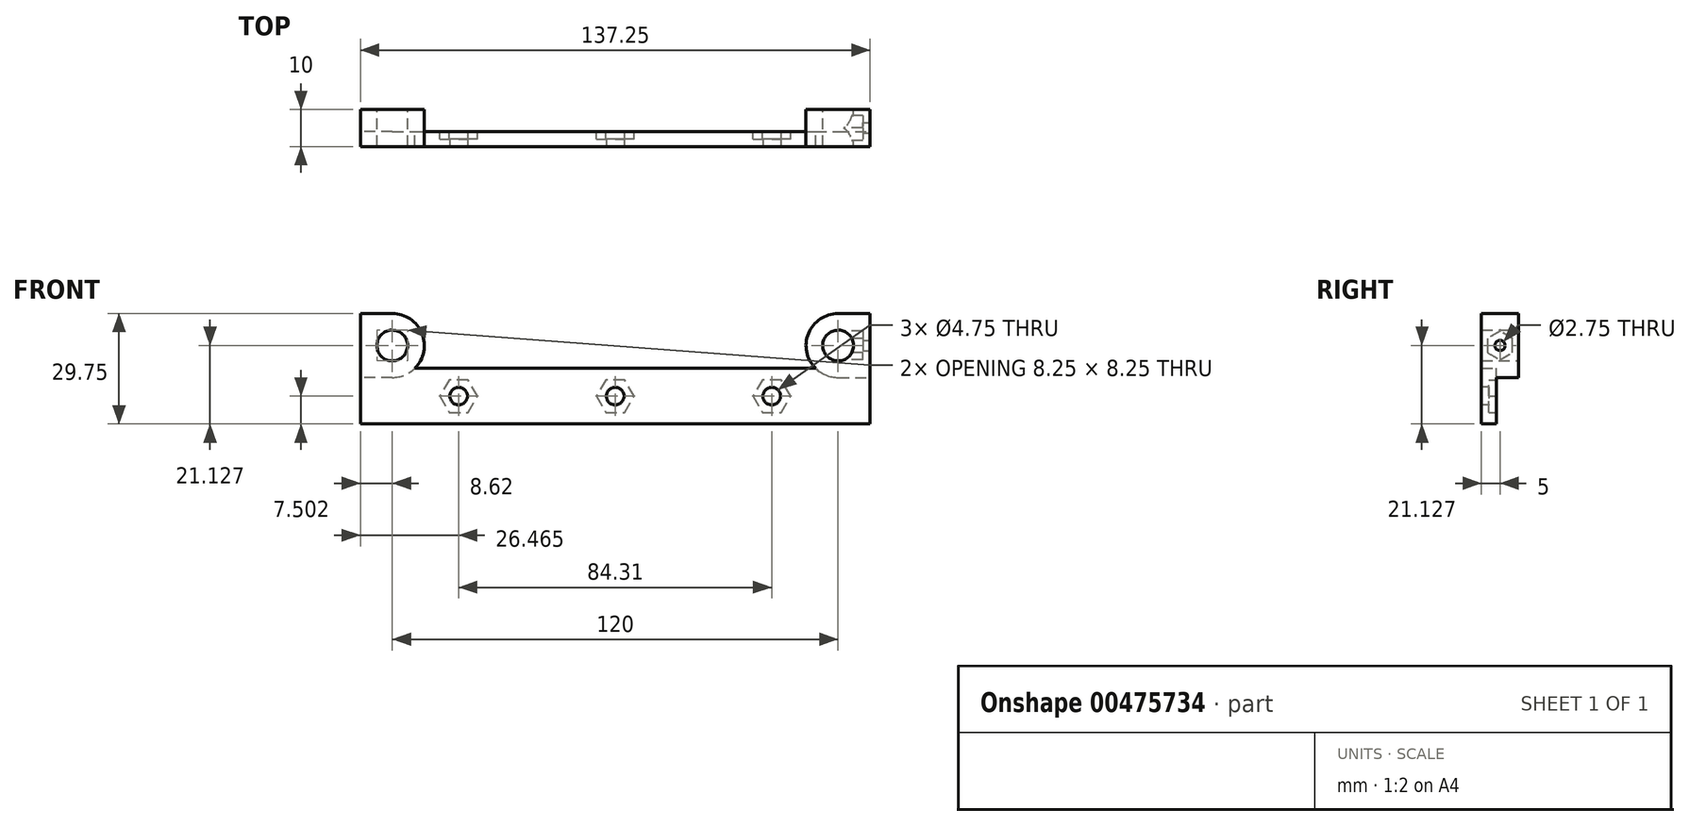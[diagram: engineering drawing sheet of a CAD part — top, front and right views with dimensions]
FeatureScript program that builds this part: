
annotation { "Feature Type Name" : "Feature", "Feature Type Description" : "" }
export const myFeature = defineFeature(function(context is Context, id is Id, definition is map)
    precondition{}
    {
        {
            var Q0;
            Q0=qCreatedBy(makeId("Front.planeOp"),FACE);
            var sketch = newSketch(context, id + "F0", { "sketchPlane" : qUnion([Q0])});
            skCircle(sketch, "E0", {"center": v(-60, 34.35) * mm, "radius": 4.12 * mm});
            skCircle(sketch, "E1", {"center": v(60, 34.35) * mm, "radius": 4.12 * mm});
            skCircle(sketch, "E2", {"center": v(-60, 34.35) * mm, "radius": 8.62 * mm});
            skCircle(sketch, "E3", {"center": v(60, 34.35) * mm, "radius": 8.62 * mm});
            skLineSegment(sketch, "E4.bottom", {"start": v(-60, 38.47) * mm, "end": v(-64.12, 38.47) * mm});
            skLineSegment(sketch, "E4.top", {"start": v(-60, 30.22) * mm, "end": v(-64.12, 30.22) * mm});
            skLineSegment(sketch, "E4.left", {"start": v(-60, 38.47) * mm, "end": v(-60, 30.22) * mm});
            skLineSegment(sketch, "E4.right", {"start": v(-64.12, 38.47) * mm, "end": v(-64.12, 30.22) * mm});
            skLineSegment(sketch, "E5.bottom", {"start": v(60, 38.47) * mm, "end": v(64.12, 38.47) * mm});
            skLineSegment(sketch, "E5.top", {"start": v(60, 30.22) * mm, "end": v(64.12, 30.22) * mm});
            skLineSegment(sketch, "E5.left", {"start": v(60, 38.47) * mm, "end": v(60, 30.22) * mm});
            skLineSegment(sketch, "E5.right", {"start": v(64.12, 38.47) * mm, "end": v(64.12, 30.22) * mm});
            skLineSegment(sketch, "E6.bottom", {"start": v(-60, 42.97) * mm, "end": v(-68.62, 42.97) * mm});
            skLineSegment(sketch, "E6.top", {"start": v(-60, 25.72) * mm, "end": v(-68.62, 25.72) * mm});
            skLineSegment(sketch, "E6.left", {"start": v(-60, 42.97) * mm, "end": v(-60, 25.72) * mm});
            skLineSegment(sketch, "E6.right", {"start": v(-68.62, 42.97) * mm, "end": v(-68.62, 25.72) * mm});
            skLineSegment(sketch, "E7.bottom", {"start": v(60, 42.97) * mm, "end": v(68.62, 42.97) * mm});
            skLineSegment(sketch, "E7.top", {"start": v(60, 25.72) * mm, "end": v(68.62, 25.72) * mm});
            skLineSegment(sketch, "E7.left", {"start": v(60, 42.97) * mm, "end": v(60, 25.72) * mm});
            skLineSegment(sketch, "E7.right", {"start": v(68.62, 42.97) * mm, "end": v(68.62, 25.72) * mm});
            skSolve(sketch);
        }
        {
            var Q0;
            Q0=qSketchRegion(id+"F0",true);
            extrude(context, id + "F1", {"entities" : qUnion([Q0]), "depth" : 5 * mm, "hasSecondDirection" : true, "secondDirectionOppositeDirection" : true, "secondDirectionDepth" : 5 * mm});
        }
        {
            var Q0;
            Q0=makeQuery(id+"F1.opExtrude","CAP_FACE",FACE,{"disambiguationData":[OSD([sQuery(id+"F0.wireOp",EDGE,"E0"),sQuery(id+"F0.wireOp",EDGE,"E2"),sQuery(id+"F0.wireOp",EDGE,"E4.bottom"),sQuery(id+"F0.wireOp",EDGE,"E4.top"),sQuery(id+"F0.wireOp",EDGE,"E4.right"),sQuery(id+"F0.wireOp",EDGE,"E6.bottom"),sQuery(id+"F0.wireOp",EDGE,"E6.top"),sQuery(id+"F0.wireOp",EDGE,"E6.right")])],"isStart":false});
            var sketch = newSketch(context, id + "F2", { "sketchPlane" : qUnion([Q0])});
            skLineSegment(sketch, "E8.bottom", {"start": v(-68.62, 13.22) * mm, "end": v(68.62, 13.22) * mm});
            skLineSegment(sketch, "E8.top", {"start": v(-68.62, 28.22) * mm, "end": v(68.62, 28.22) * mm});
            skLineSegment(sketch, "E8.left", {"start": v(-68.62, 13.22) * mm, "end": v(-68.62, 28.22) * mm});
            skLineSegment(sketch, "E8.right", {"start": v(68.62, 13.22) * mm, "end": v(68.62, 28.22) * mm});
            skSolve(sketch);
        }
        {
            var Q0;
            Q0=qSketchRegion(id+"F2",true);
            var Q1;
            Q1=makeQuery(id+"F1.opExtrude","CAP_FACE",FACE,{"disambiguationData":[OSD([sQuery(id+"F0.wireOp",EDGE,"E1"),sQuery(id+"F0.wireOp",EDGE,"E3")])],"isStart":true});
            extrude(context, id + "F3", {"entities" : qUnion([Q0]), "operationType" : NewBodyOperationType.ADD, "oppositeDirection" : true, "endBoundEntityFace" : qUnion([Q1]), "depth" : 4 * mm});
        }
        {
            var Q0;
            Q0=makeQuery(id+"F3.opExtrude","CAP_FACE",FACE,{"disambiguationData":[OSD([sQuery(id+"F2.wireOp",EDGE,"E8.bottom"),sQuery(id+"F2.wireOp",EDGE,"E8.top"),sQuery(id+"F2.wireOp",EDGE,"E8.left"),sQuery(id+"F2.wireOp",EDGE,"E8.right")])],"isStart":true});
            var sketch = newSketch(context, id + "F4", { "sketchPlane" : qUnion([Q0])});
            skCircle(sketch, "E9", {"center": v(0, 20.72) * mm, "radius": 2.38 * mm});
            skCircle(sketch, "E10", {"center": v(42.16, 20.72) * mm, "radius": 2.38 * mm});
            skCircle(sketch, "E11", {"center": v(-42.16, 20.72) * mm, "radius": 2.38 * mm});
            skLineSegment(sketch, "E12", {"start": v(0, 28.22) * mm, "end": v(0, 20.72) * mm, "construction": true});
            skLineSegment(sketch, "E13", {"start": v(0, 20.72) * mm, "end": v(0, 13.22) * mm, "construction": true});
            skSolve(sketch);
        }
        {
            var Q0;
            Q0=qSketchRegion(id+"F4",true);
            extrude(context, id + "F5", {"entities" : qUnion([Q0]), "operationType" : NewBodyOperationType.REMOVE, "endBound" : BoundingType.THROUGH_ALL, "oppositeDirection" : true, "depth" : 25 * mm});
        }
        {
            var Q0;
            Q0=makeQuery(id+"F3.opExtrude","CAP_FACE",FACE,{"disambiguationData":[OSD([sQuery(id+"F2.wireOp",EDGE,"E8.bottom"),sQuery(id+"F2.wireOp",EDGE,"E8.top"),sQuery(id+"F2.wireOp",EDGE,"E8.left"),sQuery(id+"F2.wireOp",EDGE,"E8.right")])],"isStart":false});
            var sketch = newSketch(context, id + "F6", { "sketchPlane" : qUnion([Q0])});
            skCircle(sketch, "E14.cCircle", {"center": v(0, 20.72) * mm, "radius": 4.4 * mm, "construction": true});
            skLineSegment(sketch, "E14.0", {"start": v(-2.54, 25.12) * mm, "end": v(2.54, 25.12) * mm});
            skLineSegment(sketch, "E14.1", {"start": v(2.54, 25.12) * mm, "end": v(5.08, 20.72) * mm});
            skLineSegment(sketch, "E14.2", {"start": v(5.08, 20.72) * mm, "end": v(2.54, 16.32) * mm});
            skLineSegment(sketch, "E14.3", {"start": v(2.54, 16.32) * mm, "end": v(-2.54, 16.32) * mm});
            skLineSegment(sketch, "E14.4", {"start": v(-2.54, 16.32) * mm, "end": v(-5.08, 20.72) * mm});
            skLineSegment(sketch, "E14.5", {"start": v(-5.08, 20.72) * mm, "end": v(-2.54, 25.12) * mm});
            skPoint(sketch, "E14.0.midPoint", {"position": v(0, 25.12) * mm});
            skCircle(sketch, "E15.cCircle", {"center": v(-42.16, 20.72) * mm, "radius": 4.4 * mm, "construction": true});
            skLineSegment(sketch, "E15.0", {"start": v(-44.7, 25.12) * mm, "end": v(-39.61, 25.12) * mm});
            skLineSegment(sketch, "E15.1", {"start": v(-39.61, 25.12) * mm, "end": v(-37.07, 20.72) * mm});
            skLineSegment(sketch, "E15.2", {"start": v(-37.07, 20.72) * mm, "end": v(-39.61, 16.32) * mm});
            skLineSegment(sketch, "E15.3", {"start": v(-39.61, 16.32) * mm, "end": v(-44.7, 16.32) * mm});
            skLineSegment(sketch, "E15.4", {"start": v(-44.7, 16.32) * mm, "end": v(-47.24, 20.72) * mm});
            skLineSegment(sketch, "E15.5", {"start": v(-47.24, 20.72) * mm, "end": v(-44.7, 25.12) * mm});
            skPoint(sketch, "E15.0.midPoint", {"position": v(-42.16, 25.12) * mm});
            skLineSegment(sketch, "E16", {"start": v(-42.16, 20.72) * mm, "end": v(0, 20.72) * mm, "construction": true});
            skLineSegment(sketch, "E17", {"start": v(0, 20.72) * mm, "end": v(-42.16, 20.72) * mm, "construction": true});
            skCircle(sketch, "E18.cCircle", {"center": v(42.16, 20.72) * mm, "radius": 4.4 * mm, "construction": true});
            skLineSegment(sketch, "E18.0", {"start": v(39.61, 25.12) * mm, "end": v(44.7, 25.12) * mm});
            skLineSegment(sketch, "E18.1", {"start": v(44.7, 25.12) * mm, "end": v(47.24, 20.72) * mm});
            skLineSegment(sketch, "E18.2", {"start": v(47.24, 20.72) * mm, "end": v(44.7, 16.32) * mm});
            skLineSegment(sketch, "E18.3", {"start": v(44.7, 16.32) * mm, "end": v(39.61, 16.32) * mm});
            skLineSegment(sketch, "E18.4", {"start": v(39.61, 16.32) * mm, "end": v(37.07, 20.72) * mm});
            skLineSegment(sketch, "E18.5", {"start": v(37.07, 20.72) * mm, "end": v(39.61, 25.12) * mm});
            skPoint(sketch, "E18.0.midPoint", {"position": v(42.16, 25.12) * mm});
            skLineSegment(sketch, "E19", {"start": v(0, 20.72) * mm, "end": v(42.16, 20.72) * mm, "construction": true});
            skSolve(sketch);
        }
        {
            var Q0;
            Q0=qSketchRegion(id+"F6",true);
            extrude(context, id + "F7", {"entities" : qUnion([Q0]), "operationType" : NewBodyOperationType.REMOVE, "oppositeDirection" : true, "depth" : 2 * mm});
        }
        {
            var Q0;
            Q0=makeQuery(id+"F3.opExtrude","SWEPT_FACE",FACE,{"disambiguationData":[OSD([sQuery(id+"F2.wireOp",EDGE,"E8.right")])]});
            var sketch = newSketch(context, id + "F8", { "sketchPlane" : qUnion([Q0])});
            skCircle(sketch, "E20", {"center": v(0, 34.35) * mm, "radius": 1.38 * mm});
            skLineSegment(sketch, "E21.0.0", {"start": v(5, 38.47) * mm, "end": v(5, 30.22) * mm, "construction": true});
            skLineSegment(sketch, "E21.0.1", {"start": v(5, 30.22) * mm, "end": v(-5, 30.22) * mm, "construction": true});
            skLineSegment(sketch, "E21.0.2", {"start": v(-5, 30.22) * mm, "end": v(-5, 38.47) * mm, "construction": true});
            skLineSegment(sketch, "E21.0.3", {"start": v(-5, 38.47) * mm, "end": v(5, 38.47) * mm, "construction": true});
            skPoint(sketch, "E22", {"position": v(5, 34.35) * mm});
            skSolve(sketch);
        }
        {
            var Q0;
            Q0=qSketchRegion(id+"F8",true);
            extrude(context, id + "F9", {"entities" : qUnion([Q0]), "operationType" : NewBodyOperationType.REMOVE, "endBound" : BoundingType.UP_TO_NEXT, "oppositeDirection" : true, "depth" : 25 * mm});
        }
        {
            var Q0;
            Q0=makeQuery(id+"F1.opExtrude","SWEPT_FACE",FACE,{"disambiguationData":[OSD([sQuery(id+"F0.wireOp",EDGE,"E5.right")])]});
            var sketch = newSketch(context, id + "F10", { "sketchPlane" : qUnion([Q0])});
            skCircle(sketch, "E23.cCircle", {"center": v(0, 34.35) * mm, "radius": 3.35 * mm, "construction": true});
            skLineSegment(sketch, "E23.0", {"start": v(3.35, 36.28) * mm, "end": v(3.35, 32.41) * mm});
            skLineSegment(sketch, "E23.1", {"start": v(3.35, 32.41) * mm, "end": v(0, 30.48) * mm});
            skLineSegment(sketch, "E23.2", {"start": v(0, 30.48) * mm, "end": v(-3.35, 32.41) * mm});
            skLineSegment(sketch, "E23.3", {"start": v(-3.35, 32.41) * mm, "end": v(-3.35, 36.28) * mm});
            skLineSegment(sketch, "E23.4", {"start": v(-3.35, 36.28) * mm, "end": v(0, 38.22) * mm});
            skLineSegment(sketch, "E23.5", {"start": v(0, 38.22) * mm, "end": v(3.35, 36.28) * mm});
            skPoint(sketch, "E23.0.midPoint", {"position": v(3.35, 34.35) * mm});
            skSolve(sketch);
        }
        {
            var Q0;
            Q0=qSketchRegion(id+"F10",true);
            extrude(context, id + "F11", {"entities" : qUnion([Q0]), "operationType" : NewBodyOperationType.REMOVE, "oppositeDirection" : true, "depth" : 2.5 * mm});
        }
        {
            var Q0;
            Q0=makeQuery(id+"F1.opExtrude","SWEPT_EDGE",EDGE,{"disambiguationData":[OSD([sQuery(id+"F0.wireOp",EDGE,"E5.bottom"),sQuery(id+"F0.wireOp",EDGE,"E5.right")])]});
            var Q1;
            Q1=makeQuery(id+"F1.opExtrude","SWEPT_EDGE",EDGE,{"disambiguationData":[OSD([sQuery(id+"F0.wireOp",EDGE,"E5.top"),sQuery(id+"F0.wireOp",EDGE,"E5.right")])]});
            var Q2;
            Q2=makeQuery(id+"F1.opExtrude","SWEPT_EDGE",EDGE,{"disambiguationData":[OSD([sQuery(id+"F0.wireOp",EDGE,"E4.bottom"),sQuery(id+"F0.wireOp",EDGE,"E4.right")])]});
            var Q3;
            Q3=makeQuery(id+"F1.opExtrude","SWEPT_EDGE",EDGE,{"disambiguationData":[OSD([sQuery(id+"F0.wireOp",EDGE,"E4.top"),sQuery(id+"F0.wireOp",EDGE,"E4.right")])]});
            fillet(context, id + "F12", {"entities" : qUnion([Q0, Q1, Q2, Q3]), "radius" : 4 * mm, "tangentPropagation" : true, "allowEdgeOverflow" : false});
        }
    });
